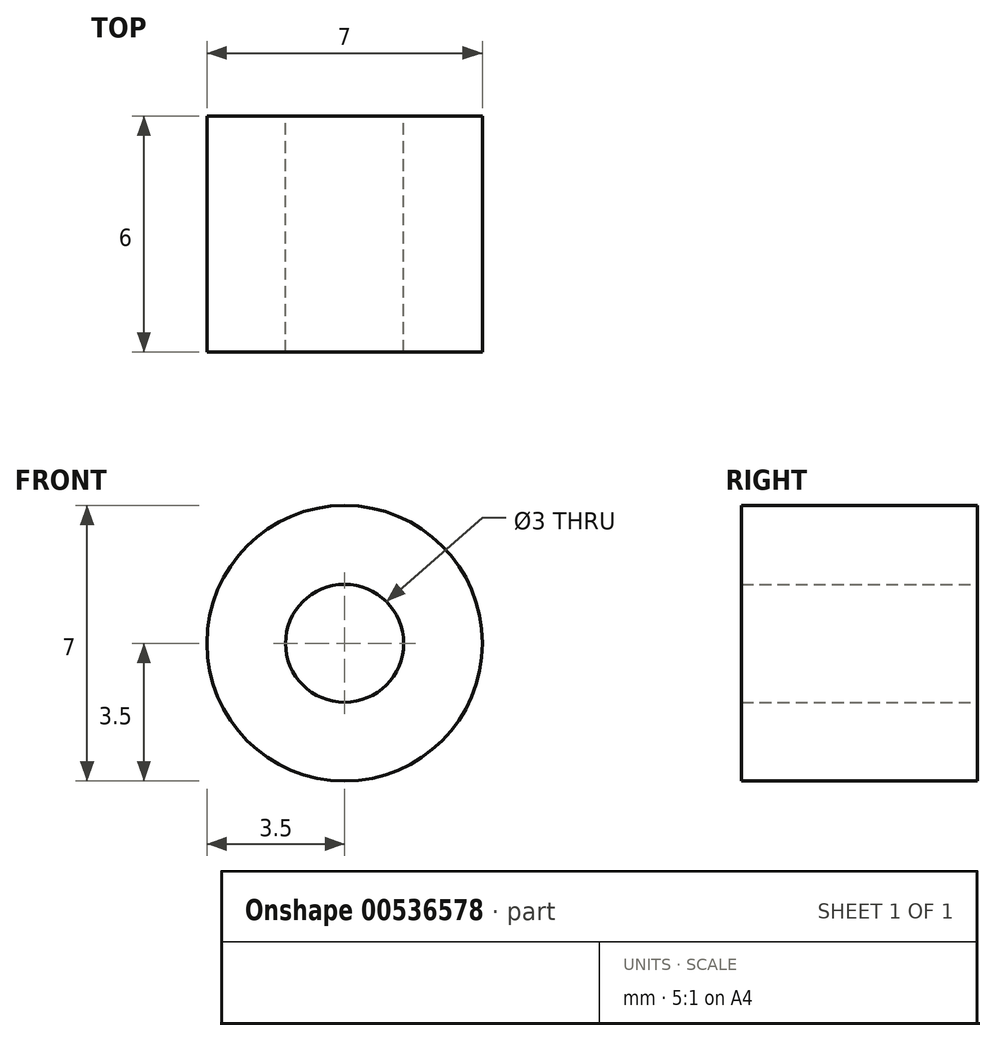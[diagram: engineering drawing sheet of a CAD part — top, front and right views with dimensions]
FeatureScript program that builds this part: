
annotation { "Feature Type Name" : "Feature", "Feature Type Description" : "" }
export const myFeature = defineFeature(function(context is Context, id is Id, definition is map)
    precondition{}
    {
        {
            var Q0;
            Q0=qCreatedBy(makeId("Front.planeOp"),FACE);
            var sketch = newSketch(context, id + "F0", { "sketchPlane" : qUnion([Q0])});
            skCircle(sketch, "E0", {"center": v(0, 0) * mm, "radius": 3.5 * mm});
            skCircle(sketch, "E1", {"center": v(0, 0) * mm, "radius": 1.5 * mm});
            skSolve(sketch);
        }
        {
            var Q0;
            Q0 = qSketchRegion(id + "F0", true);
            extrude(context, id + "F1", {"entities" : qUnion([Q0]), "endBound" : BoundingType.SYMMETRIC, "depth" : 6 * mm, "offsetDistance" : 25 * mm});
        }
    });
